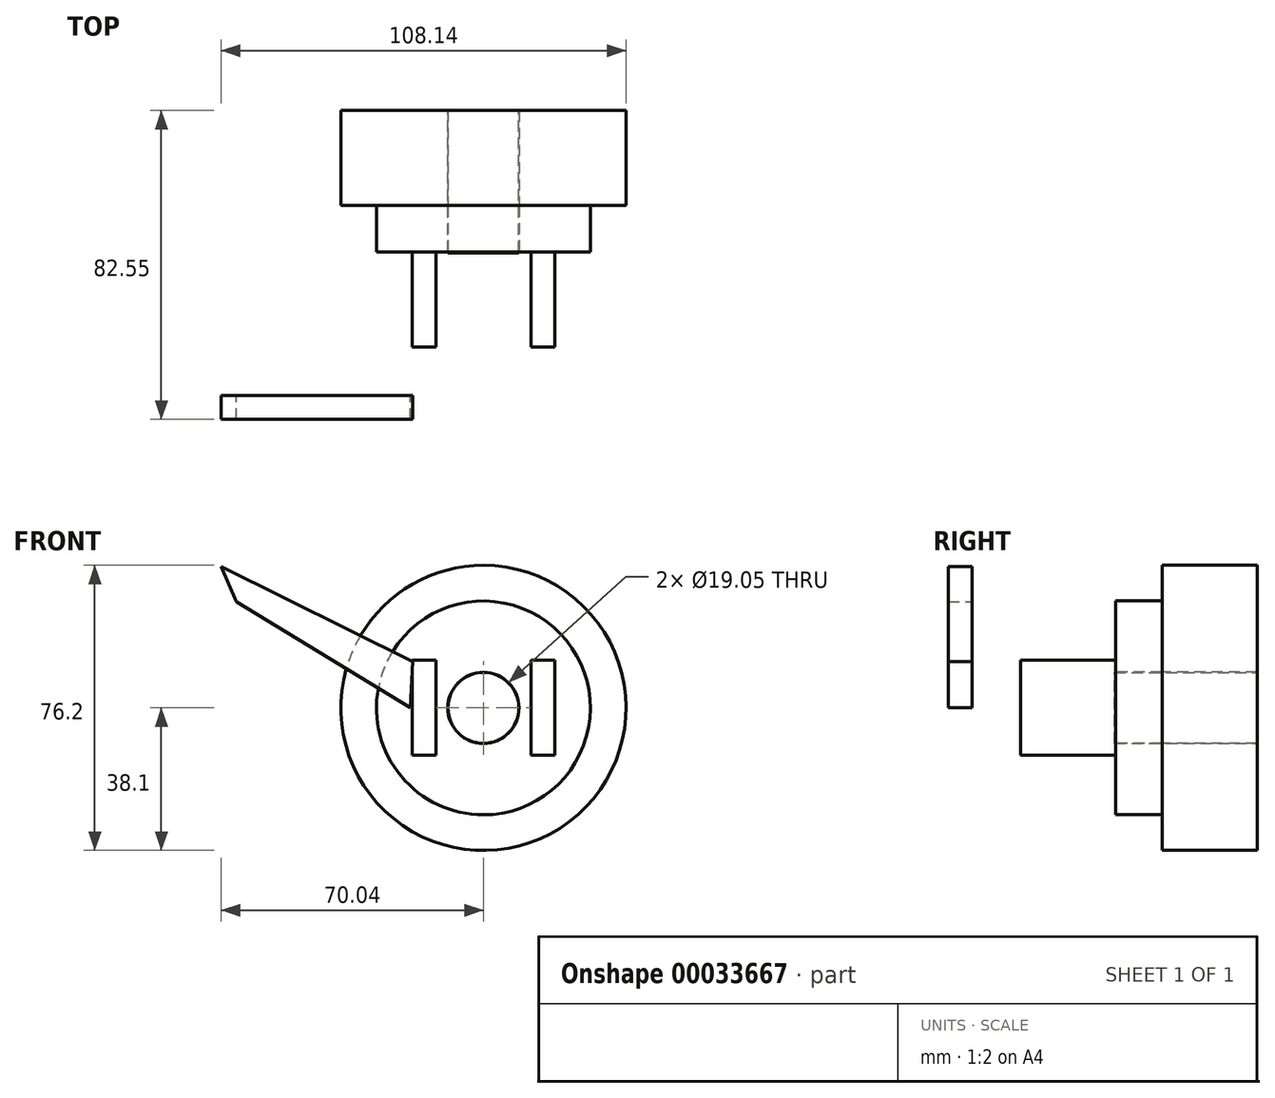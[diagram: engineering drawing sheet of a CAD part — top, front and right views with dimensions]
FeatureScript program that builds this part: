
annotation { "Feature Type Name" : "Feature", "Feature Type Description" : "" }
export const myFeature = defineFeature(function(context is Context, id is Id, definition is map)
    precondition{}
    {
        {
            var Q0;
            Q0=qCreatedBy(makeId("Right.planeOp"),FACE);
            var sketch = newSketch(context, id + "F0", { "sketchPlane" : qUnion([Q0])});
            skLineSegment(sketch, "E0.left", {"start": v(0, 17.78) * mm, "end": v(0, -17.78) * mm});
            skLineSegment(sketch, "E1.bottom", {"start": v(-25.4, 38.1) * mm, "end": v(0, 38.1) * mm});
            skLineSegment(sketch, "E1.top", {"start": v(-25.4, -38.1) * mm, "end": v(0, -38.1) * mm});
            skLineSegment(sketch, "E1.left", {"start": v(-25.4, 38.1) * mm, "end": v(-25.4, -38.1) * mm});
            skLineSegment(sketch, "E1.right", {"start": v(0, 38.1) * mm, "end": v(0, -38.1) * mm});
            skLineSegment(sketch, "E2", {"start": v(113.57, 0) * mm, "end": v(-103.08, 0) * mm});
            skSolve(sketch);
        }
        {
            var Q0;
            {var subQ5=sQuery(id+"F0.wireOp",EDGE,"E1.top");Q0=makeQuery(id+"F0.imprint","IMPRINT",FACE,{"disambiguationData":[TD([[makeQuery(id+"F0.imprint","IMPRINT",EDGE,{"derivedFrom":subQ5}),1.0]])]});}
            var Q1;
            Q1=sQuery(id+"F0.wireOp",EDGE,"E2");
            revolve(context, id + "F1", {"entities" : qUnion([Q0]), "axis" : qUnion([Q1]), "revolveType" : RevolveType.FULL});
        }
        {
            var Q0;
            Q0=qCreatedBy(makeId("Front.planeOp"),FACE);
            var sketch = newSketch(context, id + "F2", { "sketchPlane" : qUnion([Q0])});
            skLineSegment(sketch, "E3", {"start": v(0, -28.57) * mm, "end": v(0, 85.73) * mm});
            skLineSegment(sketch, "E4", {"start": v(0, -28.57) * mm, "end": v(0, -66.68) * mm});
            skCircle(sketch, "E5", {"center": v(0, 0) * mm, "radius": 9.47 * mm});
            skSolve(sketch);
        }
        {
            var Q0;
            Q0=makeQuery(id+"F1.opRevolve","SWEPT_FACE",FACE,{"disambiguationData":[OSD([sQuery(id+"F0.wireOp",EDGE,"E1.left")])]});
            var sketch = newSketch(context, id + "F3", { "sketchPlane" : qUnion([Q0])});
            skCircle(sketch, "E6", {"center": v(0, 0) * mm, "radius": 28.58 * mm});
            skSolve(sketch);
        }
        {
            var Q0;
            Q0 = qSketchRegion(id + "F2", true);
            extrude(context, id + "F4", {"entities" : qUnion([Q0]), "operationType" : NewBodyOperationType.ADD, "depth" : 38.1 * mm});
        }
        {
            var Q0;
            Q0=makeQuery(id+"F3.imprint","IMPRINT",FACE,{"disambiguationData":[TD([[makeQuery(id+"F3.imprint","IMPRINT",EDGE,{"derivedFrom":makeQuery(id+"F4.boolean.opBoolean","INTERSECT",EDGE,{"derivedFrom":[makeQuery(id+"F1.opRevolve","SWEPT_FACE",FACE,{"disambiguationData":[OSD([sQuery(id+"F0.wireOp",EDGE,"E1.left")])]}),makeQuery(id+"F4.opExtrude","SWEPT_FACE",FACE,{"disambiguationData":[OSD([sQuery(id+"F2.wireOp",EDGE,"E5")])]})]})}),1.0]])]});
            var Q1;
            Q1=makeQuery(id+"F3.imprint","IMPRINT",FACE,{"disambiguationData":[TD([[makeQuery(id+"F3.imprint","IMPRINT",EDGE,{"derivedFrom":sQuery(id+"F3.wireOp",EDGE,"E6")}),1.0]])]});
            extrude(context, id + "F5", {"entities" : qUnion([Q0, Q1]), "depth" : 12.45 * mm});
        }
        {
            var Q0;
            Q0=makeQuery(id+"F5.opExtrude","CAP_FACE",FACE,{"disambiguationData":[OSD([sQuery(id+"F3.wireOp",EDGE,"E6")])],"isStart":false});
            var sketch = newSketch(context, id + "F6", { "sketchPlane" : qUnion([Q0])});
            skCircle(sketch, "E7", {"center": v(0, 0) * mm, "radius": 9.53 * mm});
            skLineSegment(sketch, "E8.bottom", {"start": v(-19.05, 12.7) * mm, "end": v(-12.7, 12.7) * mm});
            skLineSegment(sketch, "E8.top", {"start": v(-19.05, -12.7) * mm, "end": v(-12.7, -12.7) * mm});
            skLineSegment(sketch, "E8.left", {"start": v(-19.05, 12.7) * mm, "end": v(-19.05, -12.7) * mm});
            skLineSegment(sketch, "E8.right", {"start": v(-12.7, 12.7) * mm, "end": v(-12.7, -12.7) * mm});
            skLineSegment(sketch, "E9.bottom", {"start": v(12.7, 12.7) * mm, "end": v(19.05, 12.7) * mm});
            skLineSegment(sketch, "E9.left", {"start": v(12.7, 12.7) * mm, "end": v(12.7, -12.7) * mm});
            skLineSegment(sketch, "E9.right", {"start": v(19.05, 12.7) * mm, "end": v(19.05, -12.7) * mm});
            skLineSegment(sketch, "E9.top", {"start": v(12.7, -12.7) * mm, "end": v(19.05, -12.7) * mm});
            skLineSegment(sketch, "E10", {"start": v(0, 85.04) * mm, "end": v(0, -85.04) * mm});
            skLineSegment(sketch, "E11", {"start": v(0, 0) * mm, "end": v(-94.3, 0) * mm});
            skLineSegment(sketch, "E12", {"start": v(0, 0) * mm, "end": v(87.89, 0) * mm});
            skPoint(sketch, "E13", {"position": v(-19.05, 0) * mm});
            skSolve(sketch);
        }
        {
            var Q0;
            Q0=makeQuery(id+"F6.imprint","IMPRINT",FACE,{"disambiguationData":[TD([[makeQuery(id+"F6.imprint","IMPRINT",EDGE,{"derivedFrom":sQuery(id+"F6.wireOp",EDGE,"E7")}),1.0]])]});
            extrude(context, id + "F7", {"entities" : qUnion([Q0]), "operationType" : NewBodyOperationType.REMOVE, "oppositeDirection" : true, "depth" : 118.14 * mm});
        }
        {
            var Q0;
            {var subQ0=sQuery(id+"F2.wireOp",EDGE,"E5");var subQ1=sQuery(id+"F2.wireOp",EDGE,"E3");var subQ3=makeQuery(id+"F2.imprint","INTERSECT",VERTEX,{"disambiguationData":[OD(0.0)],"derivedFrom":[subQ1,subQ0]});Q0=makeQuery(id+"F2.imprint","IMPRINT",FACE,{"disambiguationData":[TD([[makeQuery(id+"F2.imprint","IMPRINT",EDGE,{"disambiguationData":[TD([[subQ3,-1.0]])],"derivedFrom":subQ1}),-1.0]])]});}
            var Q1;
            {var subQ0=sQuery(id+"F2.wireOp",EDGE,"E5");var subQ1=sQuery(id+"F2.wireOp",EDGE,"E3");var subQ3=makeQuery(id+"F2.imprint","INTERSECT",VERTEX,{"disambiguationData":[OD(0.0)],"derivedFrom":[subQ1,subQ0]});Q1=makeQuery(id+"F2.imprint","IMPRINT",FACE,{"disambiguationData":[TD([[makeQuery(id+"F2.imprint","IMPRINT",EDGE,{"disambiguationData":[TD([[subQ3,-1.0]])],"derivedFrom":subQ1}),1.0]])]});}
            extrude(context, id + "F8", {"entities" : qUnion([Q0, Q1]), "depth" : 38.1 * mm});
        }
        {
            var Q0;
            {var subQ5=sQuery(id+"F6.wireOp",EDGE,"E8.bottom");Q0=makeQuery(id+"F6.imprint","IMPRINT",FACE,{"disambiguationData":[TD([[makeQuery(id+"F6.imprint","IMPRINT",EDGE,{"derivedFrom":subQ5}),-1.0]])]});}
            var Q1;
            {var subQ5=sQuery(id+"F6.wireOp",EDGE,"E8.top");Q1=makeQuery(id+"F6.imprint","IMPRINT",FACE,{"disambiguationData":[TD([[makeQuery(id+"F6.imprint","IMPRINT",EDGE,{"derivedFrom":subQ5}),1.0]])]});}
            var Q2;
            {var subQ5=sQuery(id+"F6.wireOp",EDGE,"E9.bottom");Q2=makeQuery(id+"F6.imprint","IMPRINT",FACE,{"disambiguationData":[TD([[makeQuery(id+"F6.imprint","IMPRINT",EDGE,{"derivedFrom":subQ5}),-1.0]])]});}
            var Q3;
            {var subQ5=sQuery(id+"F6.wireOp",EDGE,"E9.top");Q3=makeQuery(id+"F6.imprint","IMPRINT",FACE,{"disambiguationData":[TD([[makeQuery(id+"F6.imprint","IMPRINT",EDGE,{"derivedFrom":subQ5}),1.0]])]});}
            extrude(context, id + "F9", {"entities" : qUnion([Q0, Q1, Q2, Q3]), "depth" : 25.4 * mm});
        }
        {
            var Q0;
            Q0=qCreatedBy(makeId("Front.planeOp"),FACE);
            var sketch = newSketch(context, id + "F10", { "sketchPlane" : qUnion([Q0])});
            skLineSegment(sketch, "E14", {"start": v(-19.5, 0) * mm, "end": v(-65.97, 28.44) * mm});
            skLineSegment(sketch, "E15", {"start": v(-65.97, 28.44) * mm, "end": v(-70.04, 37.75) * mm});
            skLineSegment(sketch, "E16", {"start": v(-70.04, 37.75) * mm, "end": v(-18.84, 12.36) * mm});
            skLineSegment(sketch, "E17", {"start": v(-18.84, 12.36) * mm, "end": v(-19.5, 0) * mm});
            skSolve(sketch);
        }
        {
            var Q0;
            Q0=makeQuery(id+"F10.imprint","IMPRINT",FACE,{"disambiguationData":[TD([[makeQuery(id+"F10.imprint","IMPRINT",EDGE,{"derivedFrom":sQuery(id+"F10.wireOp",EDGE,"E14")}),-1.0]])]});
            extrude(context, id + "F11", {"entities" : qUnion([Q0]), "depth" : 82.55 * mm, "hasSecondDirection" : true, "secondDirectionOppositeDirection" : false, "secondDirectionDepth" : 76.2 * mm});
        }
    });
